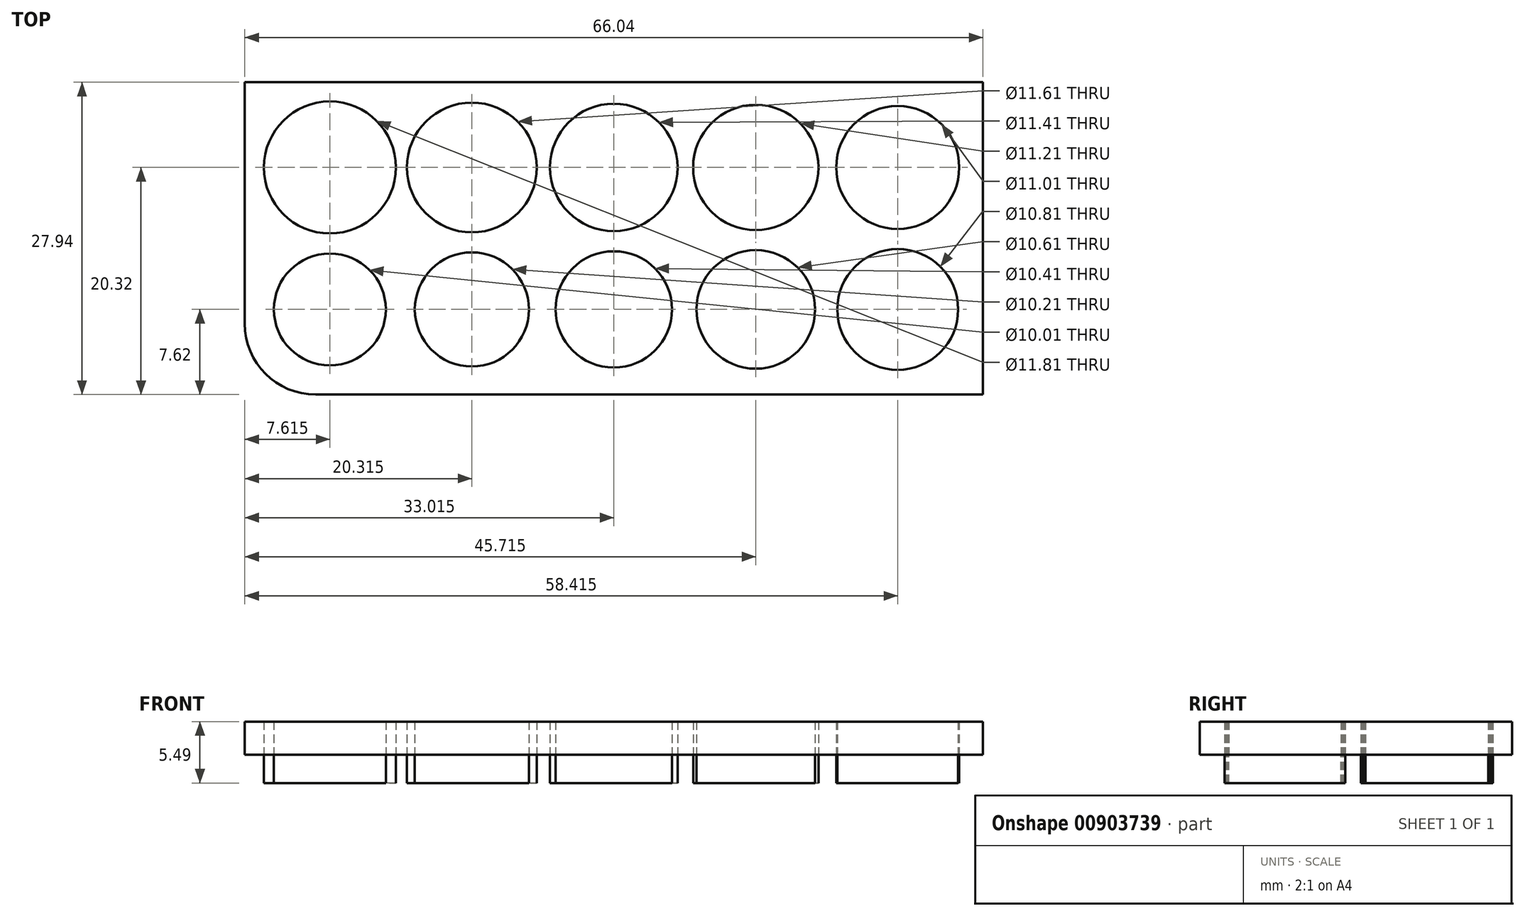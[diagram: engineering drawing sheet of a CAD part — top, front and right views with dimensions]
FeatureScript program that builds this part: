
annotation { "Feature Type Name" : "Feature", "Feature Type Description" : "" }
export const myFeature = defineFeature(function(context is Context, id is Id, definition is map)
    precondition{}
    {
        {
            var Q0;
            Q0=qCreatedBy(makeId("Top.planeOp"),FACE);
            var sketch = newSketch(context, id + "F0", { "sketchPlane" : qUnion([Q0])});
            skCircle(sketch, "E0", {"center": v(-30.57, 0) * mm, "radius": 5 * mm});
            skCircle(sketch, "E1.0.1.0", {"center": v(-30.57, 12.7) * mm, "radius": 5 * mm});
            skCircle(sketch, "E1.1.0.0", {"center": v(-17.87, 0) * mm, "radius": 5 * mm});
            skCircle(sketch, "E1.1.1.0", {"center": v(-17.87, 12.7) * mm, "radius": 5 * mm});
            skCircle(sketch, "E1.2.0.0", {"center": v(-5.17, 0) * mm, "radius": 5 * mm});
            skCircle(sketch, "E1.2.1.0", {"center": v(-5.17, 12.7) * mm, "radius": 5 * mm});
            skCircle(sketch, "E1.3.0.0", {"center": v(7.53, 0) * mm, "radius": 5 * mm});
            skCircle(sketch, "E1.3.1.0", {"center": v(7.53, 12.7) * mm, "radius": 5 * mm});
            skCircle(sketch, "E1.4.0.0", {"center": v(20.23, 0) * mm, "radius": 5 * mm});
            skCircle(sketch, "E1.4.1.0", {"center": v(20.23, 12.7) * mm, "radius": 5 * mm});
            skLineSegment(sketch, "E1.direction1", {"start": v(-30.57, 0) * mm, "end": v(-17.87, 0) * mm, "construction": true});
            skLineSegment(sketch, "E1.direction2", {"start": v(-30.57, 0) * mm, "end": v(-30.57, 12.7) * mm, "construction": true});
            skCircle(sketch, "E2.0", {"center": v(-17.87, 0) * mm, "radius": 5.1 * mm});
            skCircle(sketch, "E3.0", {"center": v(-5.17, 0) * mm, "radius": 5.2 * mm});
            skCircle(sketch, "E4.0", {"center": v(7.53, 0) * mm, "radius": 5.3 * mm});
            skCircle(sketch, "E5.0", {"center": v(20.23, 0) * mm, "radius": 5.4 * mm});
            skCircle(sketch, "E6.0", {"center": v(20.23, 12.7) * mm, "radius": 5.5 * mm});
            skCircle(sketch, "E7.0", {"center": v(7.53, 12.7) * mm, "radius": 5.6 * mm});
            skCircle(sketch, "E8.0", {"center": v(-5.17, 12.7) * mm, "radius": 5.7 * mm});
            skCircle(sketch, "E9.0", {"center": v(-17.87, 12.7) * mm, "radius": 5.8 * mm});
            skCircle(sketch, "E10.0", {"center": v(-30.57, 12.7) * mm, "radius": 5.9 * mm});
            skLineSegment(sketch, "E11.bottom", {"start": v(-38.2, 20.32) * mm, "end": v(27.85, 20.32) * mm});
            skLineSegment(sketch, "E11.top", {"start": v(-31.84, -7.62) * mm, "end": v(27.85, -7.62) * mm});
            skLineSegment(sketch, "E11.left", {"start": v(-38.2, 20.32) * mm, "end": v(-38.2, -1.27) * mm});
            skLineSegment(sketch, "E11.right", {"start": v(27.85, 20.32) * mm, "end": v(27.85, -7.62) * mm});
            skPoint(sketch, "E12.visualSharp", {"position": v(-38.2, -7.62) * mm});
            skArc(sketch, "E12.filletArc", {"start": v(-38.2, -1.27) * mm, "mid": v(-36.34, -5.76) * mm, "end": v(-31.84, -7.62) * mm});
            skSolve(sketch);
        }
        {
            var Q0;
            Q0=makeQuery(id+"F0.imprint","IMPRINT",FACE,{"disambiguationData":[TD([[makeQuery(id+"F0.imprint","IMPRINT",EDGE,{"derivedFrom":sQuery(id+"F0.wireOp",EDGE,"E0")}),-1.0]])]});
            extrude(context, id + "F1", {"entities" : qUnion([Q0]), "depth" : 2.95 * mm, "offsetDistance" : 25.4 * mm});
        }
        {
            var Q0;
            Q0=makeQuery(id+"F1.opExtrude","CAP_FACE",FACE,{"disambiguationData":[OSD([sQuery(id+"F0.wireOp",EDGE,"E0"),sQuery(id+"F0.wireOp",EDGE,"E2.0"),sQuery(id+"F0.wireOp",EDGE,"E3.0"),sQuery(id+"F0.wireOp",EDGE,"E4.0"),sQuery(id+"F0.wireOp",EDGE,"E5.0"),sQuery(id+"F0.wireOp",EDGE,"E6.0"),sQuery(id+"F0.wireOp",EDGE,"E7.0"),sQuery(id+"F0.wireOp",EDGE,"E8.0"),sQuery(id+"F0.wireOp",EDGE,"E9.0"),sQuery(id+"F0.wireOp",EDGE,"E10.0"),sQuery(id+"F0.wireOp",EDGE,"E11.bottom"),sQuery(id+"F0.wireOp",EDGE,"E11.top"),sQuery(id+"F0.wireOp",EDGE,"E11.left"),sQuery(id+"F0.wireOp",EDGE,"E11.right"),sQuery(id+"F0.wireOp",EDGE,"E12.filletArc")])],"isStart":true});
            var sketch = newSketch(context, id + "F2", { "sketchPlane" : qUnion([Q0])});
            skLineSegment(sketch, "E13.0", {"start": v(-38.2, -20.32) * mm, "end": v(27.85, -20.32) * mm});
            skLineSegment(sketch, "E14.0", {"start": v(27.85, -20.32) * mm, "end": v(27.85, 7.62) * mm});
            skLineSegment(sketch, "E15.0", {"start": v(-31.84, 7.62) * mm, "end": v(27.85, 7.62) * mm});
            skArc(sketch, "E16.0", {"start": v(-38.2, 1.27) * mm, "mid": v(-36.34, 5.76) * mm, "end": v(-31.84, 7.62) * mm});
            skLineSegment(sketch, "E17.0", {"start": v(-38.2, -20.32) * mm, "end": v(-38.2, 1.27) * mm});
            skArc(sketch, "E18.0.0", {"start": v(-31.84, 7.62) * mm, "mid": v(-36.34, 5.76) * mm, "end": v(-38.2, 1.27) * mm});
            skLineSegment(sketch, "E18.0.1", {"start": v(-38.2, 1.27) * mm, "end": v(-38.2, -20.32) * mm});
            skLineSegment(sketch, "E18.0.4", {"start": v(27.85, 7.62) * mm, "end": v(-31.84, 7.62) * mm});
            skCircle(sketch, "E19.0", {"center": v(-30.57, 0) * mm, "radius": 5 * mm});
            skCircle(sketch, "E20.0", {"center": v(-30.57, -12.7) * mm, "radius": 5.9 * mm});
            skCircle(sketch, "E21.0", {"center": v(-17.87, -12.7) * mm, "radius": 5.8 * mm});
            skCircle(sketch, "E22.0", {"center": v(-17.87, 0) * mm, "radius": 5.1 * mm});
            skCircle(sketch, "E23.0", {"center": v(-5.17, 0) * mm, "radius": 5.2 * mm});
            skCircle(sketch, "E24.0", {"center": v(-5.17, -12.7) * mm, "radius": 5.7 * mm});
            skCircle(sketch, "E25.0", {"center": v(7.53, -12.7) * mm, "radius": 5.6 * mm});
            skCircle(sketch, "E26.0", {"center": v(7.53, 0) * mm, "radius": 5.3 * mm});
            skCircle(sketch, "E27.0", {"center": v(20.23, 0) * mm, "radius": 5.4 * mm});
            skCircle(sketch, "E28.0", {"center": v(20.23, -12.7) * mm, "radius": 5.5 * mm});
            skSolve(sketch);
        }
        {
            var Q0;
            Q0=makeQuery(id+"F2.imprint","IMPRINT",FACE,{"disambiguationData":[TD([[makeQuery(id+"F2.imprint","IMPRINT",EDGE,{"derivedFrom":sQuery(id+"F2.wireOp",EDGE,"E18.0.0")}),-1.0]])]});
            var Q1;
            Q1=makeQuery(id+"F2.imprint","IMPRINT",FACE,{"disambiguationData":[TD([[makeQuery(id+"F2.imprint","IMPRINT",EDGE,{"derivedFrom":sQuery(id+"F2.wireOp",EDGE,"E19.0")}),-1.0]])]});
            var Q2;
            Q2=makeQuery(id+"F2.imprint","IMPRINT",FACE,{"disambiguationData":[TD([[makeQuery(id+"F2.imprint","IMPRINT",EDGE,{"derivedFrom":sQuery(id+"F2.wireOp",EDGE,"E22.0")}),-1.0]])]});
            var Q3;
            Q3=makeQuery(id+"F2.imprint","IMPRINT",FACE,{"disambiguationData":[TD([[makeQuery(id+"F2.imprint","IMPRINT",EDGE,{"derivedFrom":sQuery(id+"F2.wireOp",EDGE,"E23.0")}),-1.0]])]});
            var Q4;
            Q4=makeQuery(id+"F2.imprint","IMPRINT",FACE,{"disambiguationData":[TD([[makeQuery(id+"F2.imprint","IMPRINT",EDGE,{"derivedFrom":sQuery(id+"F2.wireOp",EDGE,"E26.0")}),-1.0]])]});
            var Q5;
            Q5=makeQuery(id+"F2.imprint","IMPRINT",FACE,{"disambiguationData":[TD([[makeQuery(id+"F2.imprint","IMPRINT",EDGE,{"derivedFrom":sQuery(id+"F2.wireOp",EDGE,"E27.0")}),-1.0]])]});
            var Q6;
            Q6=makeQuery(id+"F2.imprint","IMPRINT",FACE,{"disambiguationData":[TD([[makeQuery(id+"F2.imprint","IMPRINT",EDGE,{"derivedFrom":sQuery(id+"F2.wireOp",EDGE,"E28.0")}),-1.0]])]});
            var Q7;
            Q7=makeQuery(id+"F2.imprint","IMPRINT",FACE,{"disambiguationData":[TD([[makeQuery(id+"F2.imprint","IMPRINT",EDGE,{"derivedFrom":sQuery(id+"F2.wireOp",EDGE,"E25.0")}),-1.0]])]});
            var Q8;
            Q8=makeQuery(id+"F2.imprint","IMPRINT",FACE,{"disambiguationData":[TD([[makeQuery(id+"F2.imprint","IMPRINT",EDGE,{"derivedFrom":sQuery(id+"F2.wireOp",EDGE,"E24.0")}),-1.0]])]});
            var Q9;
            Q9=makeQuery(id+"F2.imprint","IMPRINT",FACE,{"disambiguationData":[TD([[makeQuery(id+"F2.imprint","IMPRINT",EDGE,{"derivedFrom":sQuery(id+"F2.wireOp",EDGE,"E21.0")}),-1.0]])]});
            var Q10;
            Q10=makeQuery(id+"F2.imprint","IMPRINT",FACE,{"disambiguationData":[TD([[makeQuery(id+"F2.imprint","IMPRINT",EDGE,{"derivedFrom":sQuery(id+"F2.wireOp",EDGE,"E20.0")}),-1.0]])]});
            extrude(context, id + "F3", {"entities" : qUnion([Q0, Q1, Q2, Q3, Q4, Q5, Q6, Q7, Q8, Q9, Q10]), "operationType" : NewBodyOperationType.ADD, "depth" : 2.54 * mm, "offsetDistance" : 25.4 * mm});
        }
    });
